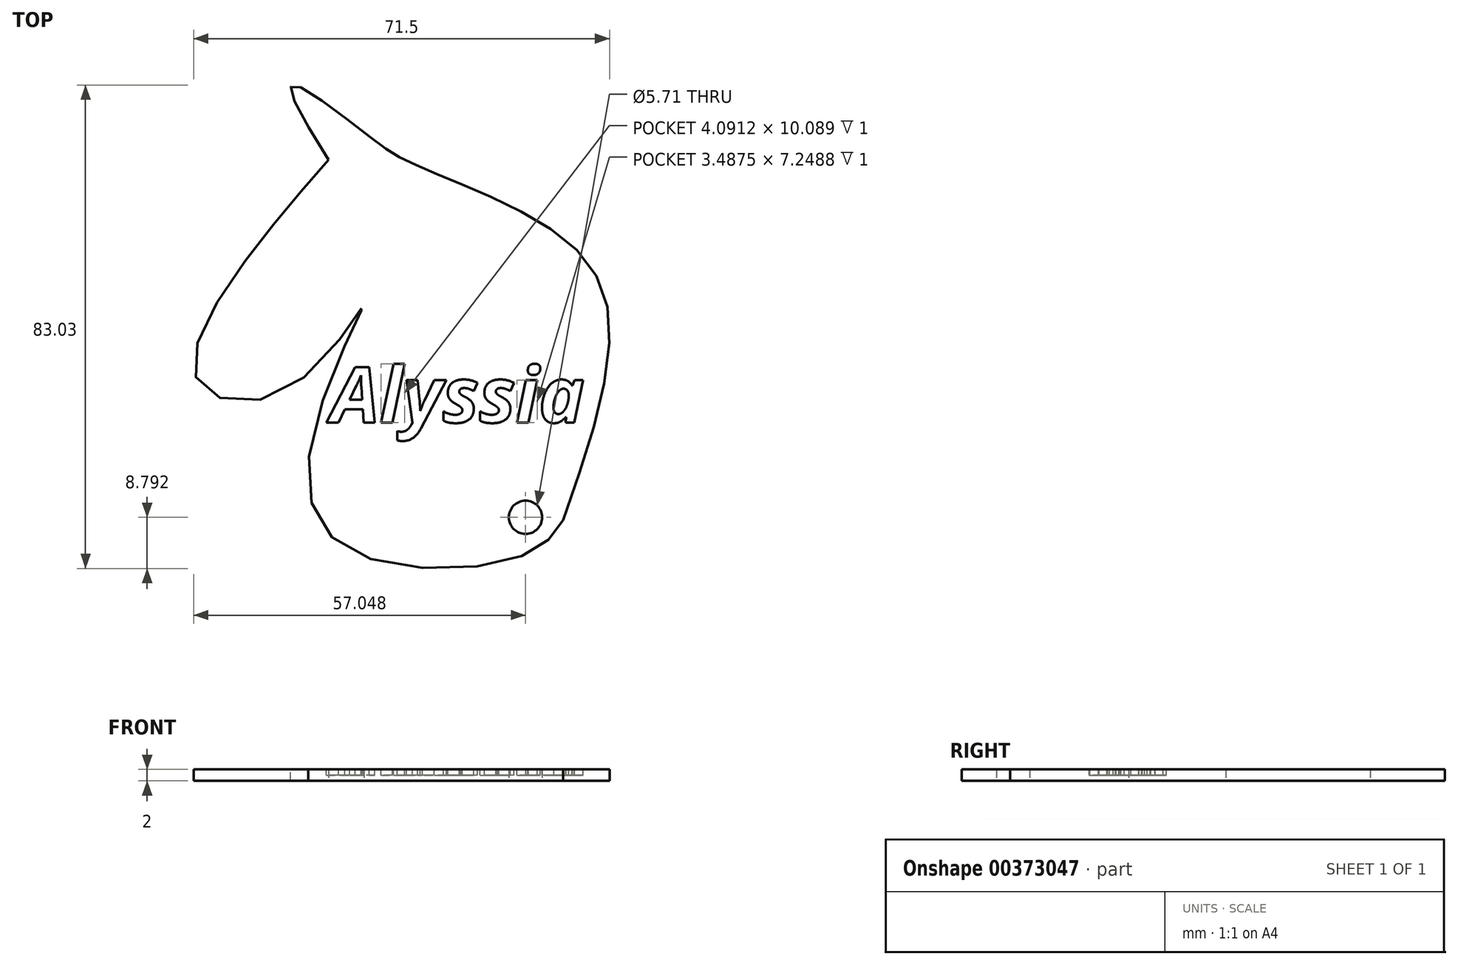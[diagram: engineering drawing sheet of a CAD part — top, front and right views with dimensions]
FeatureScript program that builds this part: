
annotation { "Feature Type Name" : "Feature", "Feature Type Description" : "" }
export const myFeature = defineFeature(function(context is Context, id is Id, definition is map)
    precondition{}
    {
        {
            var Q0;
            Q0=qCreatedBy(makeId("Top.planeOp"),FACE);
            var sketch = newSketch(context, id + "F0", { "sketchPlane" : qUnion([Q0])});
            skFitSpline(sketch, "E0", {"points": [v(-26.8, 47.68) * mm, v(-32.97, 60.49) * mm, v(-20.16, 51.95) * mm, v(-13.76, 47.68) * mm, v(0, 41.75) * mm, v(19.92, 26.33) * mm, v(13.52, -14.23) * mm], "startDerivative": vector(-87.31, 136.3) * mm, "endDerivative": vector(-66.14, -189.11) * mm});
            skFitSpline(sketch, "E1", {"points": [v(-26.8, 47.68) * mm, v(-41.8, 29.4) * mm, v(-49.5, 10) * mm, v(-33.94, 8.26) * mm, v(-20.75, 22.82) * mm, v(-29.62, 0) * mm, v(-22.9, -19.56) * mm, v(6.76, -20.25) * mm, v(13.52, -14.23) * mm], "startDerivative": vector(-108.7, -122.92) * mm, "endDerivative": vector(52.17, 79.47) * mm});
            skCircle(sketch, "E2", {"center": v(7.03, -13.74) * mm, "radius": 2.86 * mm});
            skSolve(sketch);
        }
        {
            var Q0;
            Q0 = qSketchRegion(id + "F0", true);
            extrude(context, id + "F1", {"entities" : qUnion([Q0]), "depth" : 2 * mm});
        }
        {
            var Q0;
            Q0=makeQuery(id+"F1.opExtrude","CAP_FACE",FACE,{"disambiguationData":[OSD([sQuery(id+"F0.wireOp",EDGE,"E0"),sQuery(id+"F0.wireOp",EDGE,"E1"),sQuery(id+"F0.wireOp",EDGE,"E2")])],"isStart":false});
            var sketch = newSketch(context, id + "F2", { "sketchPlane" : qUnion([Q0])});
            skText(sketch, "E3", { "text": "Alyssia\n", "fontName": "OpenSans-BoldItalic.ttf"});
            const initialGuessF2  = {"E3": [-0.0264, 0.00255, 1, 0, 0.00956]};
            skSetInitialGuess(sketch, initialGuessF2);
            skSolve(sketch);
        }
        {
            var Q0;
            Q0 = qSketchRegion(id + "F2", true);
            extrude(context, id + "F3", {"entities" : qUnion([Q0]), "operationType" : NewBodyOperationType.REMOVE, "oppositeDirection" : true, "depth" : 1 * mm});
        }
    });
